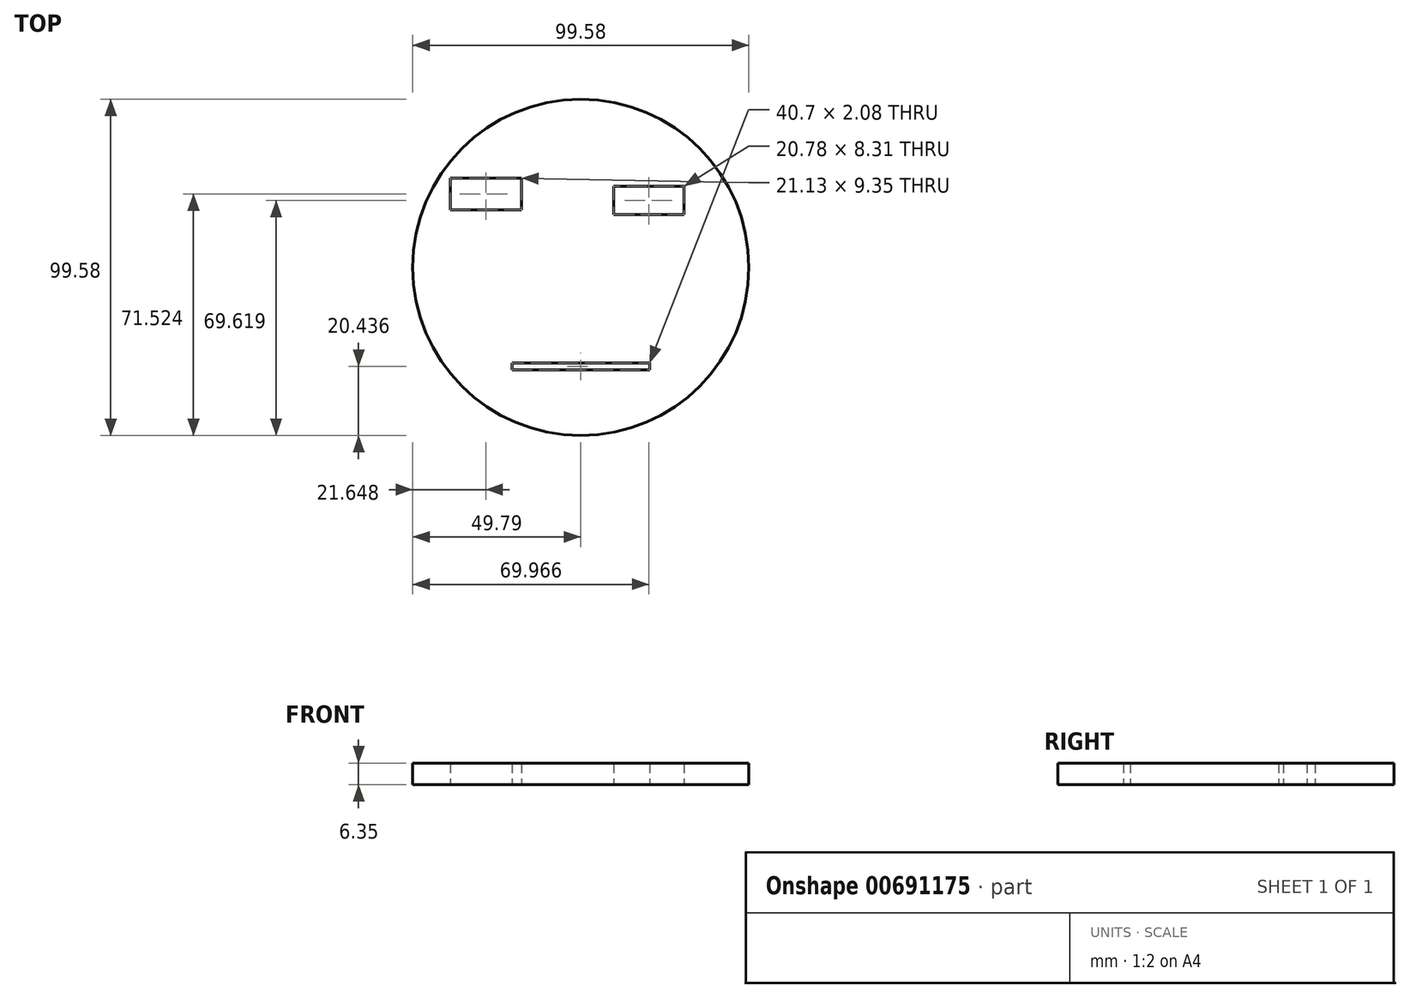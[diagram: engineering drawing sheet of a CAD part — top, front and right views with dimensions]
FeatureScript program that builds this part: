
annotation { "Feature Type Name" : "Feature", "Feature Type Description" : "" }
export const myFeature = defineFeature(function(context is Context, id is Id, definition is map)
    precondition{}
    {
        {
            var Q0;
            Q0=qCreatedBy(makeId("Top.planeOp"),FACE);
            var sketch = newSketch(context, id + "F0", { "sketchPlane" : qUnion([Q0])});
            skCircle(sketch, "E0", {"center": v(0, 0) * mm, "radius": 49.8 * mm});
            skSolve(sketch);
        }
        {
            var Q0;
            Q0=makeQuery(id+"F0.imprint","IMPRINT",FACE,{"disambiguationData":[TD([[makeQuery(id+"F0.imprint","IMPRINT",EDGE,{"derivedFrom":sQuery(id+"F0.wireOp",EDGE,"E0")}),1.0]])]});
            var sketch = newSketch(context, id + "F1", { "sketchPlane" : qUnion([Q0])});
            skLineSegment(sketch, "E1.bottom", {"start": v(-17.58, 26.41) * mm, "end": v(-38.7, 26.41) * mm});
            skLineSegment(sketch, "E1.top", {"start": v(-17.58, 17.06) * mm, "end": v(-38.7, 17.06) * mm});
            skLineSegment(sketch, "E1.left", {"start": v(-17.58, 26.41) * mm, "end": v(-17.58, 17.06) * mm});
            skLineSegment(sketch, "E1.right", {"start": v(-38.7, 26.41) * mm, "end": v(-38.7, 17.06) * mm});
            skPoint(sketch, "E1.middle", {"position": v(-28.14, 21.73) * mm});
            skLineSegment(sketch, "E2.bottom", {"start": v(38.88, 24.85) * mm, "end": v(17.75, 24.85) * mm});
            skLineSegment(sketch, "E2.top", {"start": v(38.88, 15.5) * mm, "end": v(17.75, 15.5) * mm});
            skLineSegment(sketch, "E2.left", {"start": v(38.88, 24.85) * mm, "end": v(38.88, 15.5) * mm});
            skLineSegment(sketch, "E2.right", {"start": v(17.75, 24.85) * mm, "end": v(17.75, 15.5) * mm});
            skSolve(sketch);
        }
        {
            var Q0;
            Q0=makeQuery(id+"F0.imprint","IMPRINT",FACE,{"disambiguationData":[TD([[makeQuery(id+"F0.imprint","IMPRINT",EDGE,{"derivedFrom":sQuery(id+"F0.wireOp",EDGE,"E0")}),1.0]])]});
            extrude(context, id + "F2", {"entities" : qUnion([Q0]), "depth" : 6.35 * mm, "offsetDistance" : 25.4 * mm});
        }
        {
            var Q0;
            Q0=makeQuery(id+"F1.imprint","IMPRINT",FACE,{"disambiguationData":[TD([[makeQuery(id+"F1.imprint","IMPRINT",EDGE,{"derivedFrom":sQuery(id+"F1.wireOp",EDGE,"E1.bottom")}),1.0]])]});
            var Q1;
            Q1=sQuery(id+"F1.wireOp",EDGE,"E1.right");
            var Q2;
            Q2=sQuery(id+"F1.wireOp",EDGE,"E1.bottom");
            var Q3;
            Q3=sQuery(id+"F1.wireOp",EDGE,"E1.left");
            var Q4;
            Q4=sQuery(id+"F1.wireOp",EDGE,"E1.top");
            extrude(context, id + "F3", {"entities" : qUnion([Q0]), "operationType" : NewBodyOperationType.REMOVE, "surfaceEntities" : qUnion([Q1, Q2, Q3, Q4]), "endBound" : BoundingType.THROUGH_ALL, "depth" : 6.35 * mm, "offsetDistance" : 25.4 * mm});
        }
        {
            var Q0;
            Q0=qCreatedBy(makeId("Top.planeOp"),FACE);
            var sketch = newSketch(context, id + "F4", { "sketchPlane" : qUnion([Q0])});
            skLineSegment(sketch, "E3.bottom", {"start": v(30.57, 15.67) * mm, "end": v(9.78, 15.67) * mm});
            skLineSegment(sketch, "E3.top", {"start": v(30.57, 23.99) * mm, "end": v(9.78, 23.99) * mm});
            skLineSegment(sketch, "E3.left", {"start": v(30.57, 15.67) * mm, "end": v(30.57, 23.99) * mm});
            skLineSegment(sketch, "E3.right", {"start": v(9.78, 15.67) * mm, "end": v(9.78, 23.99) * mm});
            skPoint(sketch, "E3.middle", {"position": v(20.18, 19.83) * mm});
            skSolve(sketch);
        }
        {
            var Q0;
            Q0=makeQuery(id+"F4.imprint","IMPRINT",FACE,{"disambiguationData":[TD([[makeQuery(id+"F4.imprint","IMPRINT",EDGE,{"derivedFrom":sQuery(id+"F4.wireOp",EDGE,"E3.bottom")}),-1.0]])]});
            var Q1;
            Q1=sQuery(id+"F4.wireOp",EDGE,"E3.right");
            var Q2;
            Q2=sQuery(id+"F4.wireOp",EDGE,"E3.top");
            var Q3;
            Q3=sQuery(id+"F4.wireOp",EDGE,"E3.left");
            var Q4;
            Q4=sQuery(id+"F4.wireOp",EDGE,"E3.bottom");
            extrude(context, id + "F5", {"entities" : qUnion([Q0]), "operationType" : NewBodyOperationType.REMOVE, "surfaceEntities" : qUnion([Q1, Q2, Q3, Q4]), "endBound" : BoundingType.THROUGH_ALL, "depth" : 25.15 * mm, "offsetDistance" : 25.4 * mm});
        }
        {
            var Q0;
            Q0=makeQuery(id+"F2.opExtrude","CAP_FACE",FACE,{"disambiguationData":[OSD([sQuery(id+"F0.wireOp",EDGE,"E0")])],"isStart":false});
            var sketch = newSketch(context, id + "F6", { "sketchPlane" : qUnion([Q0])});
            skLineSegment(sketch, "E4.bottom", {"start": v(21.73, -23.3) * mm, "end": v(-21.73, -23.3) * mm});
            skLineSegment(sketch, "E4.top", {"start": v(21.73, -20.52) * mm, "end": v(-21.73, -20.52) * mm});
            skLineSegment(sketch, "E4.left", {"start": v(21.73, -23.3) * mm, "end": v(21.73, -20.52) * mm});
            skLineSegment(sketch, "E4.right", {"start": v(-21.73, -23.3) * mm, "end": v(-21.73, -20.52) * mm});
            skPoint(sketch, "E4.middle", {"position": v(0, -21.9) * mm});
            skSolve(sketch);
        }
        {
            var Q0;
            Q0 = qSketchRegion(id + "F6", true);
            extrude(context, id + "F7", {"entities" : qUnion([Q0]), "operationType" : NewBodyOperationType.REMOVE, "endBound" : BoundingType.THROUGH_ALL, "depth" : 6.35 * mm, "offsetDistance" : 25.4 * mm});
        }
        {
            var Q0;
            Q0=qCreatedBy(makeId("Top.planeOp"),FACE);
            var sketch = newSketch(context, id + "F8", { "sketchPlane" : qUnion([Q0])});
            skLineSegment(sketch, "E5.bottom", {"start": v(20.35, -28.32) * mm, "end": v(-20.35, -28.32) * mm});
            skLineSegment(sketch, "E5.top", {"start": v(20.35, -30.4) * mm, "end": v(-20.35, -30.4) * mm});
            skLineSegment(sketch, "E5.left", {"start": v(20.35, -28.32) * mm, "end": v(20.35, -30.4) * mm});
            skLineSegment(sketch, "E5.right", {"start": v(-20.35, -28.32) * mm, "end": v(-20.35, -30.4) * mm});
            skPoint(sketch, "E5.middle", {"position": v(0, -29.35) * mm});
            skSolve(sketch);
        }
        {
            var Q0;
            Q0 = qSketchRegion(id + "F8", true);
            extrude(context, id + "F9", {"entities" : qUnion([Q0]), "operationType" : NewBodyOperationType.REMOVE, "endBound" : BoundingType.THROUGH_ALL, "depth" : 25.4 * mm, "offsetDistance" : 25.4 * mm});
        }
    });
